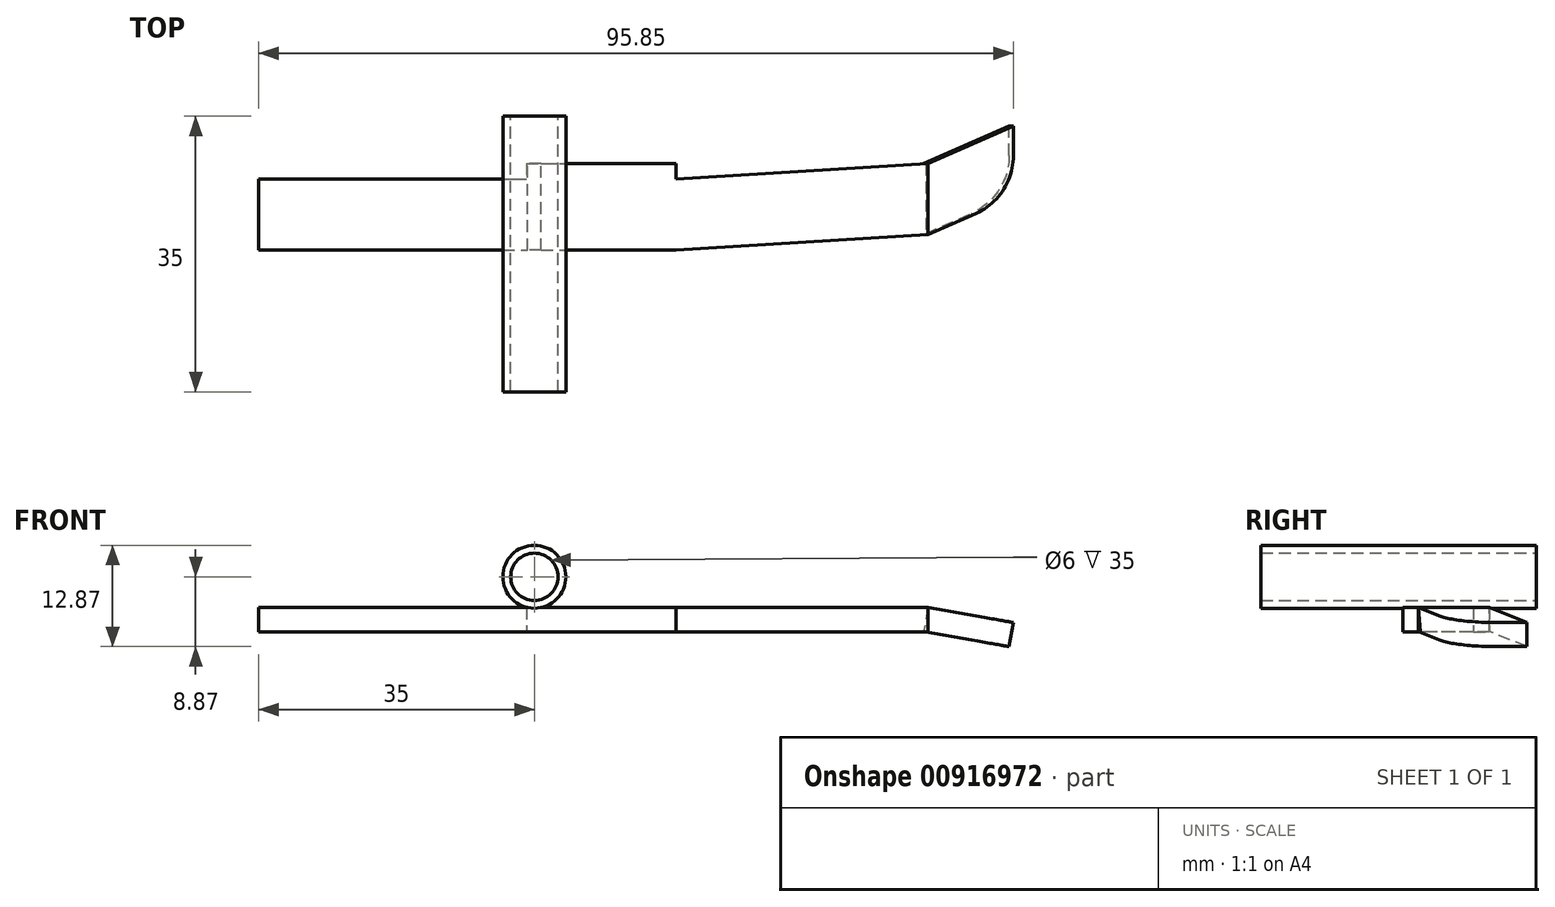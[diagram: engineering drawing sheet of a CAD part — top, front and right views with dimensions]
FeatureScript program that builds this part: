
annotation { "Feature Type Name" : "Feature", "Feature Type Description" : "" }
export const myFeature = defineFeature(function(context is Context, id is Id, definition is map)
    precondition{}
    {
        {
            var Q0;
            Q0=qCreatedBy(makeId("Front.planeOp"),FACE);
            var sketch = newSketch(context, id + "F0", { "sketchPlane" : qUnion([Q0])});
            skCircle(sketch, "E0", {"center": v(0, 0) * mm, "radius": 4 * mm});
            skCircle(sketch, "E1", {"center": v(0, 0) * mm, "radius": 3 * mm});
            skSolve(sketch);
        }
        {
            var Q0;
            Q0=qSketchRegion(id+"F0",true);
            extrude(context, id + "F1", {"entities" : qUnion([Q0]), "depth" : 35 * mm, "offsetDistance" : 25 * mm});
        }
        {
            var Q0;
            Q0=qCreatedBy(makeId("Front.planeOp"),FACE);
            cPlane(context, id + "F2", {"entities" : qUnion([Q0]), "cplaneType" : CPlaneType.OFFSET, "offset" : 17 * mm, "width" : 150 * mm, "height" : 150 * mm});
        }
        {
            var Q0;
            Q0=qCreatedBy(id+"F2.planeOp",FACE);
            var sketch = newSketch(context, id + "F3", { "sketchPlane" : qUnion([Q0])});
            skLineSegment(sketch, "E2.bottom", {"start": v(-35, 7) * mm, "end": v(50, 7) * mm});
            skLineSegment(sketch, "E2.top", {"start": v(-35, 3.9) * mm, "end": v(50, 3.9) * mm});
            skLineSegment(sketch, "E2.left", {"start": v(-35, 7) * mm, "end": v(-35, 3.9) * mm});
            skLineSegment(sketch, "E2.right", {"start": v(50, 7) * mm, "end": v(50, 3.9) * mm});
            skSolve(sketch);
        }
        {
            var Q0;
            Q0=qSketchRegion(id+"F3",true);
            extrude(context, id + "F4", {"entities" : qUnion([Q0]), "operationType" : NewBodyOperationType.ADD, "oppositeDirection" : true, "depth" : 11 * mm, "offsetDistance" : 25 * mm});
        }
        {
            var Q0;
            Q0=makeQuery(id+"F4.opExtrude","SWEPT_FACE",FACE,{"disambiguationData":[OSD([sQuery(id+"F3.wireOp",EDGE,"E2.bottom")])]});
            var sketch = newSketch(context, id + "F5", { "sketchPlane" : qUnion([Q0])});
            skLineSegment(sketch, "E3.bottom", {"start": v(-35, -6) * mm, "end": v(-1, -6) * mm});
            skLineSegment(sketch, "E3.top", {"start": v(-35, -8) * mm, "end": v(-1, -8) * mm});
            skLineSegment(sketch, "E3.left", {"start": v(-35, -6) * mm, "end": v(-35, -8) * mm});
            skLineSegment(sketch, "E3.right", {"start": v(-1, -6) * mm, "end": v(-1, -8) * mm});
            skLineSegment(sketch, "E4", {"start": v(18, -6) * mm, "end": v(18, -8) * mm});
            skLineSegment(sketch, "E5", {"start": v(18, -8) * mm, "end": v(50, -6) * mm});
            skLineSegment(sketch, "E6", {"start": v(50, -6) * mm, "end": v(18, -6) * mm});
            skLineSegment(sketch, "E7", {"start": v(18, -17) * mm, "end": v(50, -15) * mm});
            skLineSegment(sketch, "E8", {"start": v(50, -15) * mm, "end": v(50, -17) * mm});
            skLineSegment(sketch, "E9", {"start": v(50, -17) * mm, "end": v(18, -17) * mm});
            skSolve(sketch);
        }
        {
            var Q0;
            Q0=makeQuery(id+"F5.imprint","IMPRINT",FACE,{"disambiguationData":[TD([[makeQuery(id+"F5.imprint","IMPRINT",EDGE,{"derivedFrom":sQuery(id+"F5.wireOp",EDGE,"E3.bottom")}),-1.0]])]});
            var Q1;
            Q1=makeQuery(id+"F5.imprint","IMPRINT",FACE,{"disambiguationData":[TD([[makeQuery(id+"F5.imprint","IMPRINT",EDGE,{"derivedFrom":sQuery(id+"F5.wireOp",EDGE,"E4")}),1.0]])]});
            var Q2;
            Q2=makeQuery(id+"F5.imprint","IMPRINT",FACE,{"disambiguationData":[TD([[makeQuery(id+"F5.imprint","IMPRINT",EDGE,{"derivedFrom":sQuery(id+"F5.wireOp",EDGE,"E7")}),-1.0]])]});
            extrude(context, id + "F6", {"entities" : qUnion([Q0, Q1, Q2]), "operationType" : NewBodyOperationType.REMOVE, "oppositeDirection" : true, "depth" : 3.1 * mm, "offsetDistance" : 25 * mm});
        }
        {
            var Q0;
            Q0=makeQuery(id+"F4.opExtrude","SWEPT_EDGE",EDGE,{"disambiguationData":[OSD([sQuery(id+"F3.wireOp",EDGE,"E2.top"),sQuery(id+"F3.wireOp",EDGE,"E2.right")])]});
            cPlane(context, id + "F7", {"entities" : qUnion([Q0]), "cplaneType" : CPlaneType.LINE_ANGLE, "offset" : 25 * mm, "angle" : 10 * degree, "width" : 150 * mm, "height" : 150 * mm});
        }
        {
            var Q0;
            Q0=qCreatedBy(id+"F7.planeOp",FACE);
            var sketch = newSketch(context, id + "F8", { "sketchPlane" : qUnion([Q0])});
            skLineSegment(sketch, "E10", {"start": v(49.92, 15) * mm, "end": v(60.93, 10.24) * mm});
            skLineSegment(sketch, "E11", {"start": v(60.93, 10.24) * mm, "end": v(60.93, 1.24) * mm});
            skLineSegment(sketch, "E12", {"start": v(60.93, 1.24) * mm, "end": v(49.92, 6) * mm});
            skLineSegment(sketch, "E13", {"start": v(49.92, 6) * mm, "end": v(49.92, 15) * mm});
            skSolve(sketch);
        }
        {
            var Q0;
            Q0=makeQuery(id+"F8.imprint","IMPRINT",FACE,{"disambiguationData":[TD([[makeQuery(id+"F8.imprint","IMPRINT",EDGE,{"derivedFrom":sQuery(id+"F8.wireOp",EDGE,"E10")}),-1.0]])]});
            extrude(context, id + "F9", {"entities" : qUnion([Q0]), "operationType" : NewBodyOperationType.ADD, "oppositeDirection" : true, "depth" : 3.1 * mm, "offsetDistance" : 25 * mm});
        }
        {
            var Q0;
            Q0=makeQuery(id+"F9.opExtrude","SWEPT_EDGE",EDGE,{"disambiguationData":[OSD([sQuery(id+"F8.wireOp",EDGE,"E10"),sQuery(id+"F8.wireOp",EDGE,"E11")])]});
            fillet(context, id + "F10", {"entities" : qUnion([Q0]), "radius" : 8 * mm, "tangentPropagation" : true, "allowEdgeOverflow" : false});
        }
        {
            var Q0;
            Q0=qCreatedBy(makeId("Top.planeOp"),FACE);
            cPlane(context, id + "F11", {"entities" : qUnion([Q0]), "cplaneType" : CPlaneType.OFFSET, "offset" : 4 * mm, "oppositeDirection" : true, "width" : 150 * mm, "height" : 150 * mm});
        }
        {
            var Q0;
            Q0=makeQuery(id+"F1.opExtrude","SWEPT_BODY",BODY,{"disambiguationData":[OSD([sQuery(id+"F0.wireOp",EDGE,"E0"),sQuery(id+"F0.wireOp",EDGE,"E1")])]});
            var Q1;
            Q1=qCreatedBy(id+"F11.planeOp",FACE);
            mirror(context, id + "F12", {"entities" : qUnion([Q0]), "mirrorPlane" : qUnion([Q1])});
        }
        {
            var Q0;
            Q0=makeQuery(id+"F1.opExtrude","SWEPT_BODY",BODY,{"disambiguationData":[OSD([sQuery(id+"F0.wireOp",EDGE,"E0"),sQuery(id+"F0.wireOp",EDGE,"E1")])]});
            deleteBodies(context, id + "F13", {"entities" : qUnion([Q0])});
        }
    });
